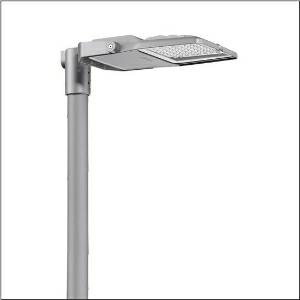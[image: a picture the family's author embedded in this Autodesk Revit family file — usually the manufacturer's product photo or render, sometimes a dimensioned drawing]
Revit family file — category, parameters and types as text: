
# Revit family: floodlight_fl_21_mini___pl61_5xa7776b4c3a_7d7f
name_source: partatom
category: Lighting Fixtures
units: mm (PartAtom-declared; Revit-internal decimal feet)

## family parameters
Cut with Voids When Loaded = No
Host = Face
Light Source = No
Part Type = Normal
Room Calculation Point = No
Round Connector Dimension = Use Diameter
Shared = No

## types (1)
- --- (1 x LED, 6360 lm, 45.7 W, 4000K)
    Apparent Load = 46 VA
    CIE Flux Codes = 33 65 98 100 100
    Color Rendering = 70
    Color Temperature = 4000K
    Default Elevation = 1800 mm
    Description = Floodlight FL 21 mini, floodlight, primary light control with lens, of PMMA, primary optical cover: protective disc, of toughened safety glass, transparent, light distribution: PL61, light emission: direct distribution, installation type: surface-mounted, LED, High Power LED, rated luminous flux: 6.360lm, luminous efficacy: 139lm/W, light colour: 740, colour temperature: 4000K, control gear: D4iSmart Interface (Zhaga), control: overheat protection, constant luminous flux control, time-dependent luminous flux control, flexible luminous flux parameterisation, pre-setting: logarithmic dimming characteristic, with terminal, 6-pole, mains connection: 220..240V, AC, 50/60Hz, start of lifetime: 46W, end of service life: 48W, reduction: 22W, mast bracket, of diecast aluminium, powder-coated, Siteco® metallic grey (DB 702S), corrosivity category C5 mid according to DIN EN ISO 12944, suitable for swimming pools, chlorine-resistant, sealing non-destructively replaceable, mast bracket, of steel, galvanised, powder-coated, Siteco® metallic grey (DB 702S), Smart Interface below and above, protection rating (complete): IP66, insulation class (complete): insulation class II (safety insulation), certification: CE, ENEC, VDE, protection symbol: D, impact resistance: IK08, permissible operating ambient temperature: -40..+40°C, permissible operating ambient temperature for outdoor applications: -40..+50°C, standard: DIN EN 12944, LABS conformity tested according to VDMA 24364:2018-05, packaging unit: 1 piece

Light Distribution: PL61
    Height = 70 mm
    Lamp = 1 x LED
    Lamp Light Flux = 6360 lm
    Lamp Power = 45.7 W
    Lamp count = 1
    Length = 485 mm
    Luminous efficacy = 139 lm/W
    Manufacturer = Siteco
    ModVariant = No
    Model = 5XA7776B4C3A
    Number of Poles = 1
    OnlyDefault = Yes
    Power Factor = 1
    Product Name = Floodlight FL 21 mini | PL61
    Product group = floodlight | pylon annexe
    ProductGroupID = 6200
    Protection Class = Protection class II
    Protection Degree = IP 66
    RLX_Detail_Level = 1
    RLX_Emergency_Light_Flux = 0 lm
    RLX_Emergency_Type = 0
    RLX_Emergency_Type_DB = No
    RlxData = <blob elided: 101045 chars, md5=11825b73>
    Socket = socket
    Standby Power = 0 W
    System Light Flux = 6360 lm
    System Power = 46 W
    Type Comments = factory setting: luminous flux: 100 % | dim-lin: 254 | 463 mA
    Type Image = l_1007125.jpg
    URL = http://relux.com
    VarID = @adj_100612
    Voltage = 0 V
    Weight = 0.00 kg
    Width = 337 mm

## geometry (parser evidence)
native form markers: Blend x4, Sweep x11
no freeform markers — native parametric forms only
